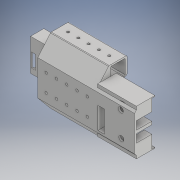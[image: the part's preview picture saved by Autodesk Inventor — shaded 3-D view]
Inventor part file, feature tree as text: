
AUTODESK INVENTOR PART (.ipt)
format: ipt  version: 2017 (Build 210142000, 142)  size: 656,896 bytes
history: native  units: mm
features: extrude x30, sketch x29
ambient origin geometry x8: Origin, YZ Plane, XZ Plane, XY Plane, X Axis, Y Axis, Z Axis, Center Point
bodies: Solid1 (feature_tree)
feature tree (59):
  extrude  "Extrusion1"  Depth=17.0mm
  extrude  "Extrusion2"  Depth=30.3mm
  extrude  "Extrusion32"  Depth=16.75mm
  extrude  "Extrusion33"  Depth=1.55mm
  extrude  "Extrusion34"  Depth=1.75mm
  extrude  "Extrusion35"  Depth=56.3mm TaperAngle=0.0deg
  extrude  "Extrusion36"  Depth=17.7mm
  extrude  "Extrusion37"  Depth=30.3mm
  extrude  "Extrusion38"  Depth=17.0mm
  extrude  "Extrusion39"  Depth=3.01mm
  extrude  "Extrusion40"  Depth=3.01mm
  extrude  "Extrusion41"  Depth=3.0mm
  extrude  "Extrusion42"  Depth=3.0mm
  extrude  "Extrusion43"  Depth=6.0mm
  extrude  "Extrusion44"  Depth=4.9105mm TaperAngle=0.0deg
  extrude  "Extrusion46"  Depth=29.6mm TaperAngle=0.0deg
  extrude  "Extrusion47"  Depth=5.45mm
  extrude  "Extrusion48"  Depth=2.611mm
  extrude  "Extrusion49"  Depth=12.5mm
  extrude  "Extrusion50"  Depth=29.6mm TaperAngle=0.0deg
  extrude  "Extrusion54"  Depth=8.0mm
  extrude  "Extrusion57"  Depth=8.0mm
  extrude  "Extrusion58"  Depth=29.6mm TaperAngle=0.0deg
  extrude  "Extrusion59"  Depth=12.5mm
  extrude  "Extrusion60"  Depth=18.5228mm
  extrude  "Extrusion61"  Depth=10.411mm
  extrude  "Extrusion62"  Depth=7.678mm TaperAngle=0.0deg
  extrude  "Extrusion63"  Depth=9.468mm
  extrude  "Extrusion64"  Depth=20.215mm
  extrude  "Extrusion65"  Depth=3.0mm
  sketch  "Sketch1"  dims[d1=17.0mm d3=17.7mm]
  sketch  "Sketch2"  dims[d4=30.3mm d5=16.5mm]
  sketch  "Sketch35"  dims[d6=16.75mm d7=11.61105mm]
  sketch  "Sketch36"  dims[d9=56.3mm d10=0.0mm d11=1.55mm]
  sketch  "Sketch37"  dims[d15=1.75mm d16=14.4375mm]
  sketch  "Sketch38"  dims[d17=14.438mm d19=56.3mm d20=0.0mm]
  sketch  "Sketch39"  dims[d186=11.61105mm d187=17.7mm]
  sketch  "Sketch40"  dims[d188=30.3mm d189=16.5mm]
  sketch  "Sketch41"  dims[d191=15.034681mm d192=17.0mm]
  sketch  "Sketch42"  dims[d193=8.062mm d194=0.0mm d195=3.01mm]
  sketch  "Sketch43"  dims[d196=3.01mm d197=3.01mm]
  sketch  "Sketch44"  dims[d198=3.0mm d200=3.0mm]
  sketch  "Sketch45"  dims[d201=0.0mm d202=3.0mm]
  sketch  "Sketch46"  dims[d203=6.0mm d204=6.0mm]
  sketch  "Sketch47"  dims[d205=8.062mm d206=0.0mm d207=4.9105mm d208=0.0mm]
  sketch  "Sketch49"  dims[d209=4.9105mm d210=0.0mm d211=29.6mm d212=0.0mm]
  sketch  "Sketch50"  dims[d213=6.11mm d214=5.45mm]
  sketch  "Sketch51"  dims[d215=1.466mm d216=2.611mm]
  sketch  "Sketch52"  dims[d217=12.5mm d218=10.105mm]
  sketch  "Sketch57"  dims[d219=13.239mm d220=29.6mm d221=0.0mm]
  sketch  "Sketch60"  dims[d222=9.3mm d223=8.0mm]
  sketch  "Sketch61"  dims[d224=8.0mm d225=11.75mm]
  sketch  "Sketch62"  dims[d227=22.65mm d228=29.6mm d229=0.0mm]
  sketch  "Sketch63"  dims[d230=12.5mm d231=7.078mm]
  sketch  "Sketch64"  dims[d232=13.358mm d237=18.5228mm]
  sketch  "Sketch65"  dims[d238=5.4544mm d239=10.411mm]
  sketch  "Sketch66"  dims[d240=7.678mm d241=29.6mm d242=0.0mm]
  sketch  "Sketch67"  dims[d243=0.0mm d244=9.468mm]
  sketch  "Sketch68"  dims[d245=4.388mm d246=20.215mm d247=17.3148mm d248=29.6mm d249=0.0mm d250=37.662mm d251=0.0mm d252=37.662mm d253=0.0mm d254=37.662mm d255=0.0mm d256=37.662mm d257=0.0mm d260=22.938mm d261=0.0mm d262=3.0mm d263=64.3mm d264=3.0mm d265=3.0mm d266=6.0mm d267=6.0mm d268=22.938mm d269=0.0mm d270=12.0mm d271=0.0mm d272=0.7mm d273=14.3mm d274=0.0mm d275=5.0mm d276=5.0mm d277=5.0mm d278=0.0mm d288=15.1mm d289=3.94mm d291=1.04mm d292=14.5mm d293=18.0mm d294=0.0mm d295=1.75mm d296=0.85mm d297=15.034681mm d308=3.923631mm d309=3.923631mm d316=15.584681mm d320=1.0mm d324=1.0mm d325=1.0mm d336=4.65065mm d338=0.0mm d339=0.0mm d340=0.25mm d341=0.0mm d342=1.5mm d343=0.0mm d344=0.75mm d345=3.0mm d346=0.0mm d347=1.5mm d348=0.0mm d349=0.75mm d350=3.0mm d351=0.0mm d353=2.43332mm d354=7.374mm d355=7.374486mm d356=8.15mm d357=2.43332mm d359=7.34mm d360=2.433mm d361=10.0mm d362=7.34mm d363=2.4332mm d364=10.0mm d365=7.34mm d366=2.4332mm d367=10.0mm d368=8.15mm d369=10.0mm d370=3.0mm d371=0.0mm d372=2.43332mm d374=8.125mm d375=2.4332mm d376=2.4332mm d377=2.4332mm d378=2.4332mm d379=10.0mm d380=8.125mm d381=10.0mm d382=8.125mm d383=10.0mm d384=8.125mm d385=10.0mm d386=8.125mm d387=8.15mm d388=8.15mm d389=3.0mm d390=0.0mm d391=2.4332mm d392=8.15mm d393=8.125mm d394=10.0mm d395=3.0mm d396=0.0mm d397=12.225mm d399=13.225mm d400=12.225mm d406=1.0mm d407=12.7mm d408=12.7mm d409=0.5mm d410=0.5mm d411=12.7mm d412=12.7mm d413=0.5mm d414=2.4332mm d415=8.15mm d416=34.0mm d417=8.5mm d418=50.0mm d420=10.0mm d421=20.0mm d423=17.0mm d426=3.0mm d427=0.0mm]
